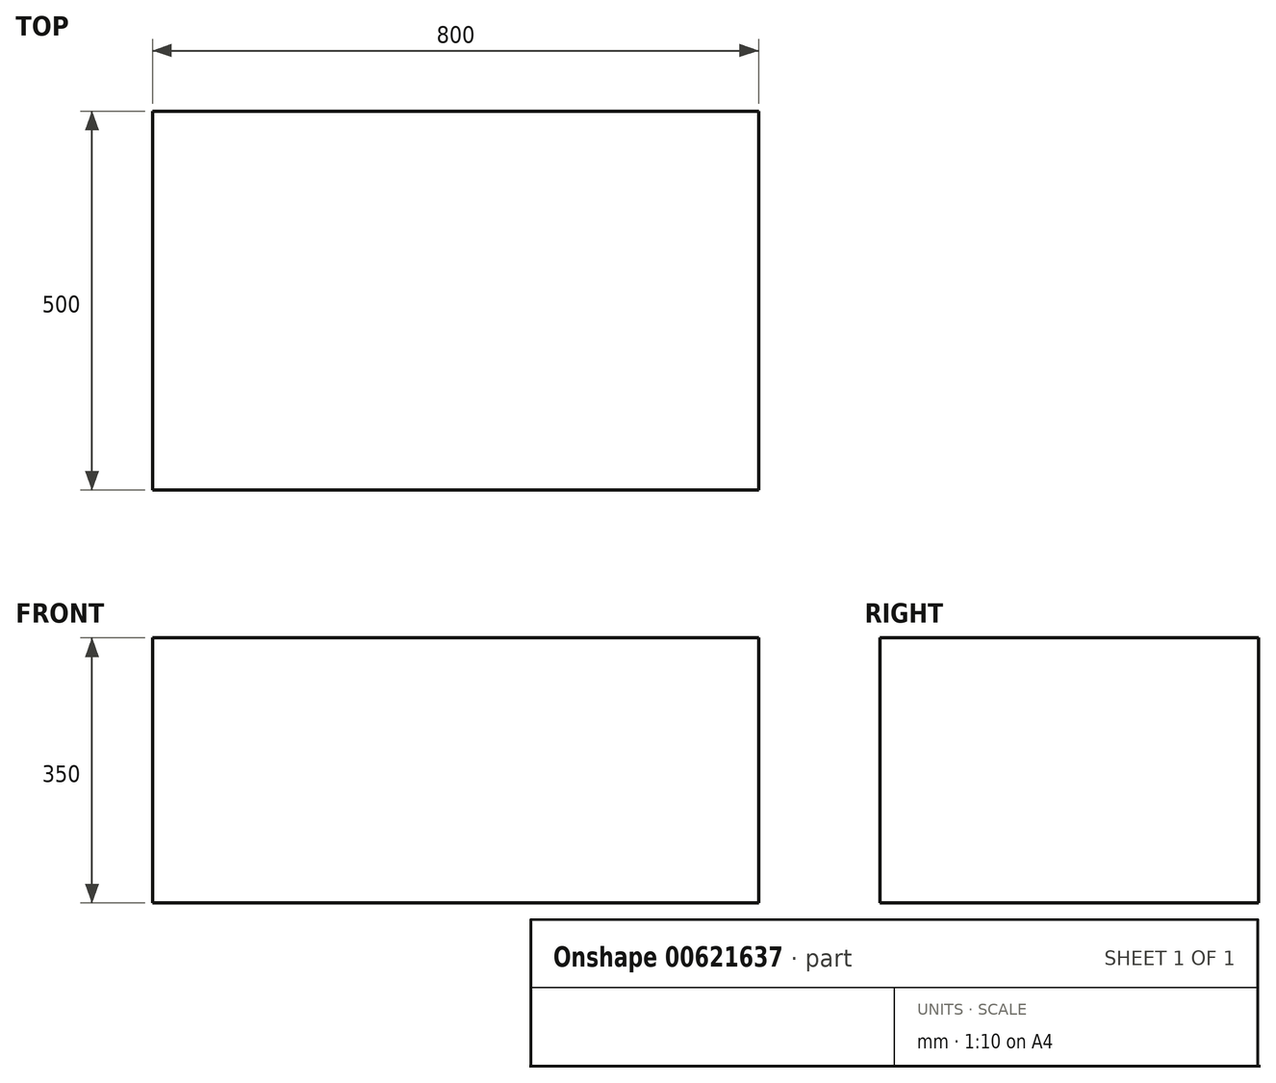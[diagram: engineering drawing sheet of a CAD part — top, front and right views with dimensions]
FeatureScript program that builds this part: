
annotation { "Feature Type Name" : "Feature", "Feature Type Description" : "" }
export const myFeature = defineFeature(function(context is Context, id is Id, definition is map)
    precondition{}
    {
        {
            var Q0;
            Q0=qCreatedBy(makeId("Top.planeOp"),FACE);
            var sketch = newSketch(context, id + "F0", { "sketchPlane" : qUnion([Q0])});
            skLineSegment(sketch, "E0.bottom", {"start": v(400, 250) * mm, "end": v(-400, 250) * mm});
            skLineSegment(sketch, "E0.top", {"start": v(400, -250) * mm, "end": v(-400, -250) * mm});
            skLineSegment(sketch, "E0.left", {"start": v(400, 250) * mm, "end": v(400, -250) * mm});
            skLineSegment(sketch, "E0.right", {"start": v(-400, 250) * mm, "end": v(-400, -250) * mm});
            skPoint(sketch, "E0.middle", {"position": v(0, 0) * mm});
            skSolve(sketch);
        }
        {
            var Q0;
            Q0=makeQuery(id+"F0.imprint","IMPRINT",FACE,{"disambiguationData":[TD([[makeQuery(id+"F0.imprint","IMPRINT",EDGE,{"derivedFrom":sQuery(id+"F0.wireOp",EDGE,"E0.bottom")}),1.0]])]});
            extrude(context, id + "F1", {"entities" : qUnion([Q0]), "oppositeDirection" : true, "depth" : 350 * mm, "offsetDistance" : 25 * mm});
        }
    });
